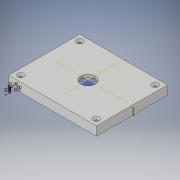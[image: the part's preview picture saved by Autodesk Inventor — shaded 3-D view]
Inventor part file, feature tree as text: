
AUTODESK INVENTOR PART (.ipt)
format: ipt  version: 2019 (Build 230136000, 136)  size: 156,672 bytes
history: native  units: in
note: dims shown in document units (in); Inventor stores cm internally (conversion verified against a paired STEP export)
features: sketch x5, extrude x4, plane x2, mirror x2, chamfer x1
ambient origin geometry x8: Origin, YZ Plane, XZ Plane, XY Plane, X Axis, Y Axis, Z Axis, Center Point
bodies: Solid1 (feature_tree)
feature tree (14):
  extrude  "Extrusion1"  Depth=2.808in
  extrude  "Extrusion2"  Depth=0.14in
  extrude  "Extrusion3"  Depth=0.14in
  sketch  "Sketch5"  dims[d6=0.25in d7=0.0in d8=3.088in]
  extrude  "Extrusion6"  Depth=3.088in
  chamfer  "Chamfer1"  Distance=0.14in
  plane  "Work Plane4"
  plane  "Work Plane5"
  mirror  "Mirror3"
  mirror  "Mirror4"
  sketch  "Sketch1"  dims[d0=3.535in d1=2.808in]
  sketch  "Sketch2"  dims[d2=0.14in d3=0.14in]
  sketch  "Sketch3"  dims[d4=0.14in d5=0.14in]
  sketch  "Sketch7"  dims[d9=3.815in d10=0.14in d11=0.0in d12=1.9075in d13=1.544in d14=0.629in d15=0.14in d16=0.04in d17=0.0in d18=0.0in d19=0.05in d20=0.3in d21=0.2405in d22=0.2in d23=0.03in d40=0.1065in d41=0.2465in d42=1.0in d43=0.0in d44=0.075in d45=0.125in d46=0.3367in d47=-1.9075in d48=-1.544in]
